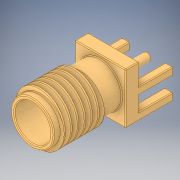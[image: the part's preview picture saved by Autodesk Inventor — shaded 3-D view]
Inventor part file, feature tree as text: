
AUTODESK INVENTOR PART (.ipt)
format: ipt  version: 2019 (Build 230136000, 136)  size: 492,032 bytes
history: native  units: in
note: dims shown in document units (in); Inventor stores cm internally (conversion verified against a paired STEP export)
features: fillet x1
ambient origin geometry x8: Origin, YZ Plane, XZ Plane, XY Plane, X Axis, Y Axis, Z Axis, Center Point
bodies: Solid1 (feature_tree)
feature tree (1):
  fillet  "Fillet1"  [1 undecoded]
note: 1 required parameter value undecoded (feature->parameter linkage not recoverable at this tier; creation-order binding heuristic only, values carry confidence <= 0.55)
